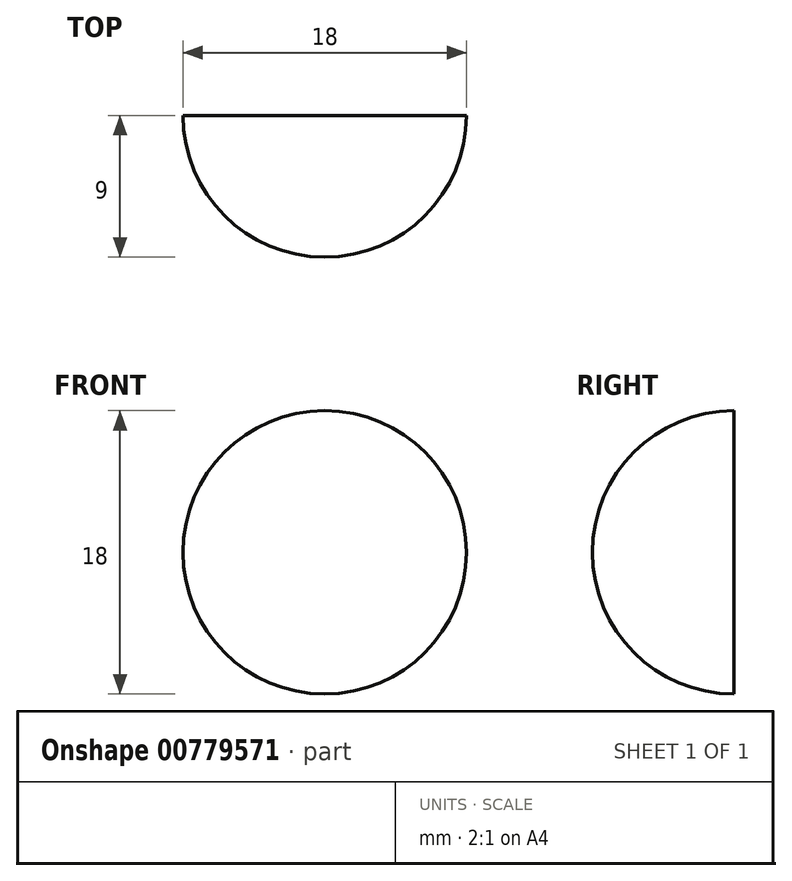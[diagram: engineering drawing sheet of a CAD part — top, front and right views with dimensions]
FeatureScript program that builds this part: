
annotation { "Feature Type Name" : "Feature", "Feature Type Description" : "" }
export const myFeature = defineFeature(function(context is Context, id is Id, definition is map)
    precondition{}
    {
        {
            var Q0;
            Q0=qCreatedBy(makeId("Front.planeOp"),FACE);
            var sketch = newSketch(context, id + "F0", { "sketchPlane" : qUnion([Q0])});
            skArc(sketch, "E0", {"start": v(0, -9) * mm, "mid": v(9, 0) * mm, "end": v(0, 9) * mm});
            skLineSegment(sketch, "E1", {"start": v(0, 15.23) * mm, "end": v(0, -11.98) * mm});
            skArc(sketch, "E2", {"start": v(35.23, -9) * mm, "mid": v(44.23, 0) * mm, "end": v(35.23, 9) * mm});
            skLineSegment(sketch, "E3", {"start": v(35.23, 15.23) * mm, "end": v(35.23, -11.98) * mm});
            skSolve(sketch);
        }
        {
            var Q0;
            Q0=sQuery(id+"F0.wireOp",EDGE,"E0");
            var Q1;
            Q1=sQuery(id+"F0.wireOp",EDGE,"E1");
            revolve(context, id + "F1", {"bodyType" : ToolBodyType.SURFACE, "surfaceOperationType" : NewSurfaceOperationType.NEW, "surfaceEntities" : qUnion([Q0]), "axis" : qUnion([Q1]), "revolveType" : RevolveType.ONE_DIRECTION, "angle" : 180 * degree});
        }
    });
